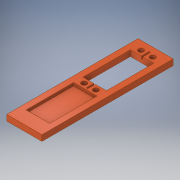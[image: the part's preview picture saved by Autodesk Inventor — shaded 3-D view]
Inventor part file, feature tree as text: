
AUTODESK INVENTOR PART (.ipt)
format: ipt  version: 2017 (Build 210142000, 142)  size: 157,696 bytes
history: native  units: mm
features: extrude x5, sketch x4
ambient origin geometry x8: Origin, YZ Plane, XZ Plane, XY Plane, X Axis, Y Axis, Z Axis, Center Point
bodies: Solid1 (feature_tree)
feature tree (9):
  extrude  "Extrusion1"  Depth=112.0mm
  sketch  "Sketch2"  dims[d2=5.0mm d3=0.0mm]
  extrude  "Extrusion2"  TaperAngle=0.0deg  [1 undecoded]
  extrude  "Extrusion3"  Depth=20.0mm
  extrude  "Extrusion4"  Depth=11.5mm
  extrude  "Extrusion5"  Depth=5.0mm
  sketch  "Sketch1"  dims[d0=30.0mm d1=112.0mm]
  sketch  "Sketch3"  dims[d4=5.0mm d5=20.0mm]
  sketch  "Sketch4"  dims[d6=40.5mm d7=11.5mm d8=5.0mm d9=0.0mm d10=2.5mm d11=0.0mm d13=4.0mm d14=4.0mm d15=2.75mm d16=2.75mm d17=4.5mm d18=2.5mm d19=0.0mm d20=6.5mm d21=1.2mm d22=2.0mm d23=0.0mm]
note: 1 required parameter value undecoded (feature->parameter linkage not recoverable at this tier; creation-order binding heuristic only, values carry confidence <= 0.55)
